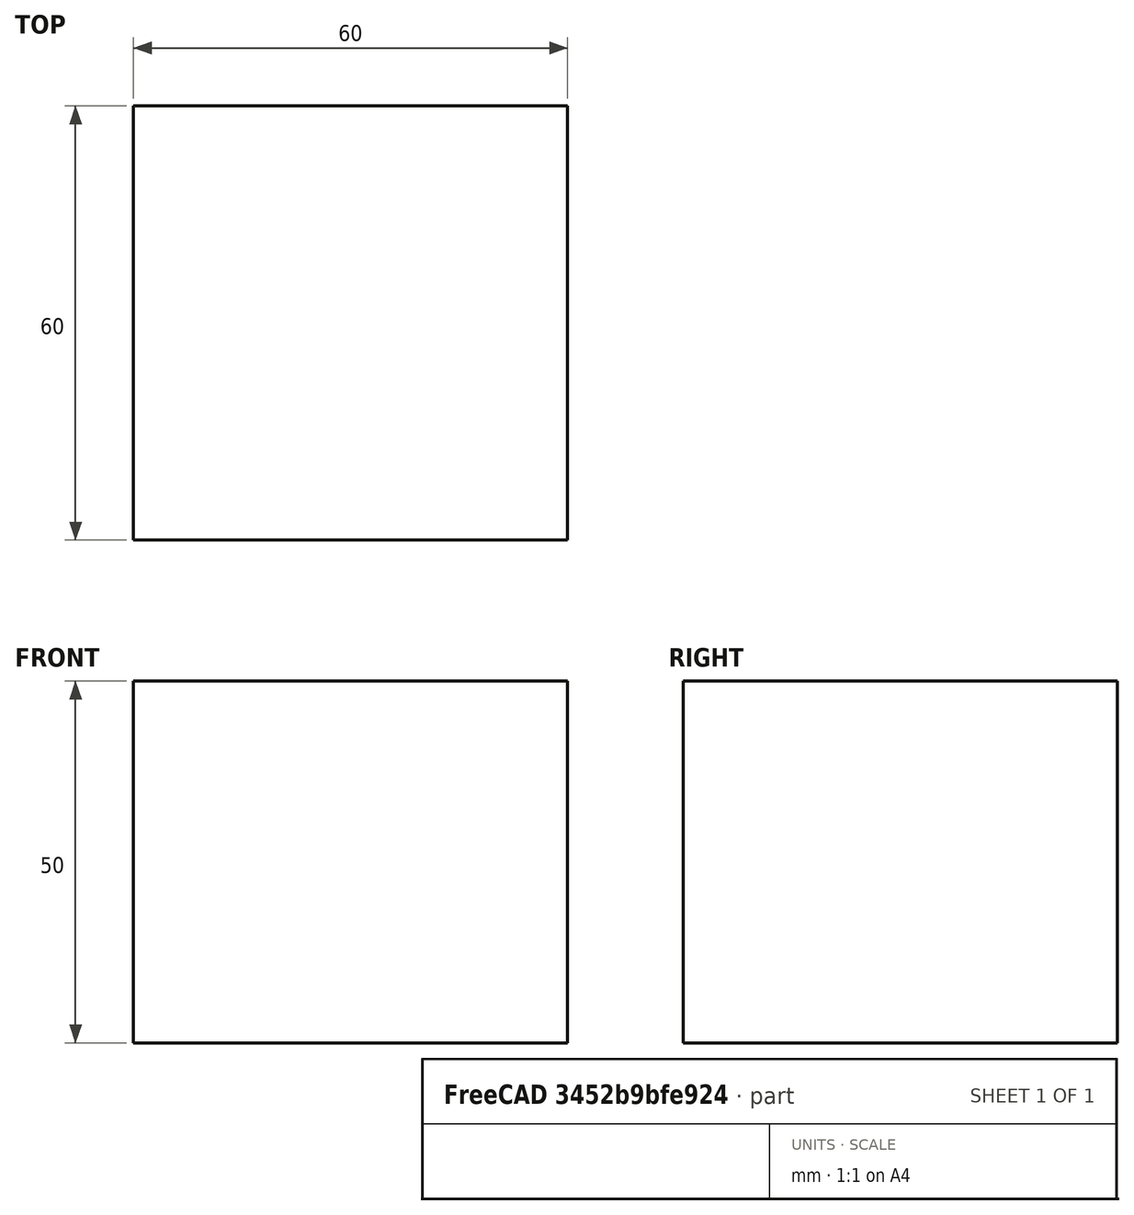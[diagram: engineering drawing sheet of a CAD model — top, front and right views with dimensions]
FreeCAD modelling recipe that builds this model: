
FCSTD DOCUMENT  (FreeCAD 0.18R16110 (Git))
Label: cad3
License: All rights reserved
LicenseURL: http://en.wikipedia.org/wiki/All_rights_reserved
objects: Sketcher::SketchObject×6, App::Part×1, Part::Extrusion×1
note: 7 computed .brp shape members not serialized (recipe doc carries the construction recipe); baked Part::Feature solids carry a one-line shape summary decoded from their .brp

FEATURE [App::Part] Part
  Origin = -> Origin
FEATURE [Sketcher::SketchObject] Sketch
  sketch-geometry (4):
    g0: LineSegment StartX=-49.991 StartY=39.6069 StartZ=0 EndX=10.009 EndY=39.6069 EndZ=0
    g1: LineSegment StartX=10.009 StartY=39.6069 StartZ=0 EndX=10.009 EndY=-20.3931 EndZ=0
    g2: LineSegment StartX=10.009 StartY=-20.3931 StartZ=0 EndX=-49.991 EndY=-20.3931 EndZ=0
    g3: LineSegment StartX=-49.991 StartY=-20.3931 StartZ=0 EndX=-49.991 EndY=39.6069 EndZ=0
  constraints (10):
    c: Coincident(g0,g1)
    c: Coincident(g1,g2)
    c: Coincident(g2,g3)
    c: Coincident(g3,g0)
    c: Horizontal(g0)
    c: Horizontal(g2)
    c: Vertical(g1)
    c: Vertical(g3)
    c: DistanceX(g2,g1) = 60
    c: DistanceY(g2,g0) = 60
FEATURE [Part::Extrusion] Extrude
  Base = -> Sketch
  Dir = (0,0,1)
  DirMode = 2
  FaceMakerClass = Part::FaceMakerBullseye
  LengthFwd = 50
  LengthRev = 0
  Solid = true
  Symmetric = false
FEATURE [Sketcher::SketchObject] Sketch001
  sketch-geometry (10):
    g0: LineSegment StartX=-25.5776 StartY=18.5583 StartZ=0 EndX=-44.7711 EndY=34.6139 EndZ=0
    g1: LineSegment StartX=-44.7711 StartY=34.6139 StartZ=0 EndX=-44.7711 EndY=16.8639 EndZ=0
    g2: LineSegment StartX=-44.8845 StartY=-15.398 StartZ=0 EndX=-44.8845 EndY=2.35198 EndZ=0
    g3: LineSegment StartX=-44.8845 StartY=16.8639 StartZ=0 EndX=-34.7711 EndY=16.6378 EndZ=0
    g4: LineSegment StartX=-34.7711 StartY=16.6378 StartZ=0 EndX=-34.7711 EndY=11.6378 EndZ=0
    g5: LineSegment StartX=-34.9027 StartY=11.6378 StartZ=0 EndX=-39.7711 EndY=11.6378 EndZ=0
    g6: LineSegment StartX=-39.7711 StartY=11.6378 StartZ=0 EndX=-39.7711 EndY=7.39443 EndZ=0
    g7: LineSegment StartX=-39.7711 StartY=7.39443 StartZ=0 EndX=-34.7711 EndY=7.00041 EndZ=0
    g8: LineSegment StartX=-34.7711 StartY=7.00041 StartZ=0 EndX=-34.7711 EndY=2.00041 EndZ=0
    g9: LineSegment StartX=-34.7711 StartY=2.00041 StartZ=0 EndX=-44.7711 EndY=2.00041 EndZ=0
  constraints (22):
    c: Coincident(g0,g1)
    c: Vertical(g1)
    c: DistanceY(g1,g0) = 17.75
    c: Vertical(g2)
    c: DistanceY(g2,g2) = 17.75
    c: Coincident(g3,g4)
    c: Vertical(g4)
    c: DistanceX(g1,g3) = 10
    c: DistanceY(g4,g3) = 5
    c: Horizontal(g5)
    c: DistanceX(g5,g4) = 5
    c: DistanceY(g5,g3) = 5
    c: Coincident(g5,g6)
    c: Vertical(g6)
    c: Coincident(g6,g7)
    c: Coincident(g7,g8)
    c: Vertical(g8)
    c: Coincident(g8,g9)
    c: Horizontal(g9)
    c: DistanceX(g6,g7) = 5
    c: DistanceX(g9,g8) = 10
    c: DistanceY(g8,g7) = 5
FEATURE [Sketcher::SketchObject] Sketch002
  sketch-geometry (26):
    g0: LineSegment StartX=-44.7203 StartY=34.5946 StartZ=0 EndX=5.27972 EndY=34.5946 EndZ=0
    g1: LineSegment StartX=-45 StartY=-15.9054 StartZ=0 EndX=5 EndY=-15.9054 EndZ=0
    g2: GeomPoint X=10.0268 Y=39.5882 Z=0
    g3: GeomPoint X=10.0865 Y=-20.4118 Z=0
    g4: GeomPoint X=-49.9762 Y=39.0946 Z=0
    g5: GeomPoint X=-49.9135 Y=-20.9054 Z=0
    g6: LineSegment StartX=-44.9602 StartY=34.859 StartZ=0 EndX=-44.9602 EndY=16.8446 EndZ=0
    g7: LineSegment StartX=-44.9602 StartY=16.8446 StartZ=0 EndX=-34.9602 EndY=16.8446 EndZ=0
    g8: LineSegment StartX=-34.9602 StartY=16.8446 StartZ=0 EndX=-34.9602 EndY=11.8446 EndZ=0
    g9: LineSegment StartX=-34.9602 StartY=11.8446 StartZ=0 EndX=-39.9602 EndY=11.8446 EndZ=0
    g10: LineSegment StartX=-39.9602 StartY=11.8446 StartZ=0 EndX=-39.9602 EndY=7.39695 EndZ=0
    g11: LineSegment StartX=-39.9602 StartY=7.39695 StartZ=0 EndX=-34.9602 EndY=6.84462 EndZ=0
    g12: LineSegment StartX=-34.9602 StartY=6.84462 StartZ=0 EndX=-34.9602 EndY=1.84462 EndZ=0
    g13: LineSegment StartX=-34.9602 StartY=1.84462 StartZ=0 EndX=-44.9602 EndY=1.84462 EndZ=0
    g14: LineSegment StartX=-45 StartY=1.8818 StartZ=0 EndX=-45 EndY=-15.9054 EndZ=0
    g15: LineSegment StartX=5 StartY=-15.9054 StartZ=0 EndX=5 EndY=1.84462 EndZ=0
    g16: LineSegment StartX=5 StartY=1.84462 StartZ=0 EndX=-5 EndY=1.84462 EndZ=0
    g17: LineSegment StartX=-5 StartY=1.84462 StartZ=0 EndX=-5 EndY=6.84462 EndZ=0
    g18: LineSegment StartX=-5 StartY=6.84462 StartZ=0 EndX=0 EndY=6.84462 EndZ=0
    g19: LineSegment StartX=0 StartY=11.8446 StartZ=0 EndX=-5 EndY=11.8446 EndZ=0
    g20: LineSegment StartX=5.07817 StartY=14.9948 StartZ=0 EndX=5.2122 EndY=14.7105 EndZ=0
    g21: LineSegment StartX=4.97323 StartY=14.7105 StartZ=0 EndX=5.2234 EndY=34.6516 EndZ=0
    g22: LineSegment StartX=0 StartY=6.84462 StartZ=0 EndX=0 EndY=11.8446 EndZ=0
    g23: LineSegment StartX=0 StartY=11.9798 StartZ=0 EndX=-5 EndY=11.8446 EndZ=0
    g24: LineSegment StartX=-5 StartY=11.8446 StartZ=0 EndX=-5 EndY=16.8446 EndZ=0
    g25: LineSegment StartX=-5 StartY=16.8446 StartZ=0 EndX=5 EndY=16.8446 EndZ=0
  constraints (61):
    c: Horizontal(g0)
    c: DistanceX(g0,g0) = 50
    c: Horizontal(g1)
    c: DistanceX(g1,g1) = 50
    c: DistanceY(g3,g2) = 60
    c: DistanceY(g5,g4) = 60
    c: DistanceX(g5,g3) = 60
    c: Vertical(g6)
    c: DistanceY(g6,g0) = 17.75
    c: Coincident(g6,g7)
    c: Horizontal(g7)
    c: DistanceX(g6,g7) = 10
    c: Coincident(g7,g8)
    c: Vertical(g8)
    c: DistanceY(g8,g7) = 5
    c: Coincident(g8,g9)
    c: Horizontal(g9)
    c: Coincident(g9,g10)
    c: Vertical(g10)
    c: Coincident(g10,g11)
    c: DistanceX(g9,g8) = 5
    c: DistanceX(g10,g11) = 5
    c: DistanceY(g11,g8) = 5
    c: Coincident(g11,g12)
    c: Vertical(g12)
    c: Coincident(g12,g13)
    c: Horizontal(g13)
    c: DistanceY(g12,g11) = 5
    c: DistanceX(g13,g12) = 10
    c: Coincident(g14,g1)
    c: Vertical(g14)
    c: DistanceY(g1,g13) = 17.75
    c: DistanceY(g5,g1) = 5
    c: Coincident(g1,g15)
    c: Vertical(g15)
    c: DistanceY(g1,g15) = 17.75
    c: Coincident(g15,g16)
    c: Horizontal(g16)
    c: DistanceX(g16,g15) = 10
    c: Coincident(g16,g17)
    c: Vertical(g17)
    c: DistanceY(g16,g17) = 5
    c: Coincident(g17,g18)
    c: PointOnObject(g18,g-2)
    c: DistanceX(g17,g18) = 5
    c: PointOnObject(g19,g-2)
    c: Horizontal(g19)
    c: DistanceY(g18,g17) = 0
    c: Coincident(g18,g22)
    c: Vertical(g22)
    c: DistanceY(g18,g22) = 5
    c: Coincident(g23,g19)
    c: DistanceX(g19,g22) = 5
    c: Coincident(g19,g24)
    c: Vertical(g24)
    c: Coincident(g24,g25)
    c: PointOnObject(g25,g21)
    c: Horizontal(g25)
    c: DistanceX(g24,g25) = 10
    c: DistanceY(g19,g24) = 5
    c: DistanceY(g25,g0) = 17.75
FEATURE [Sketcher::SketchObject] Sketch003
FEATURE [Sketcher::SketchObject] Sketch004
  Placement = pos=(0,0,0) rot=(-1,0,0;4.71239rad)
FEATURE [Sketcher::SketchObject] Sketch005
